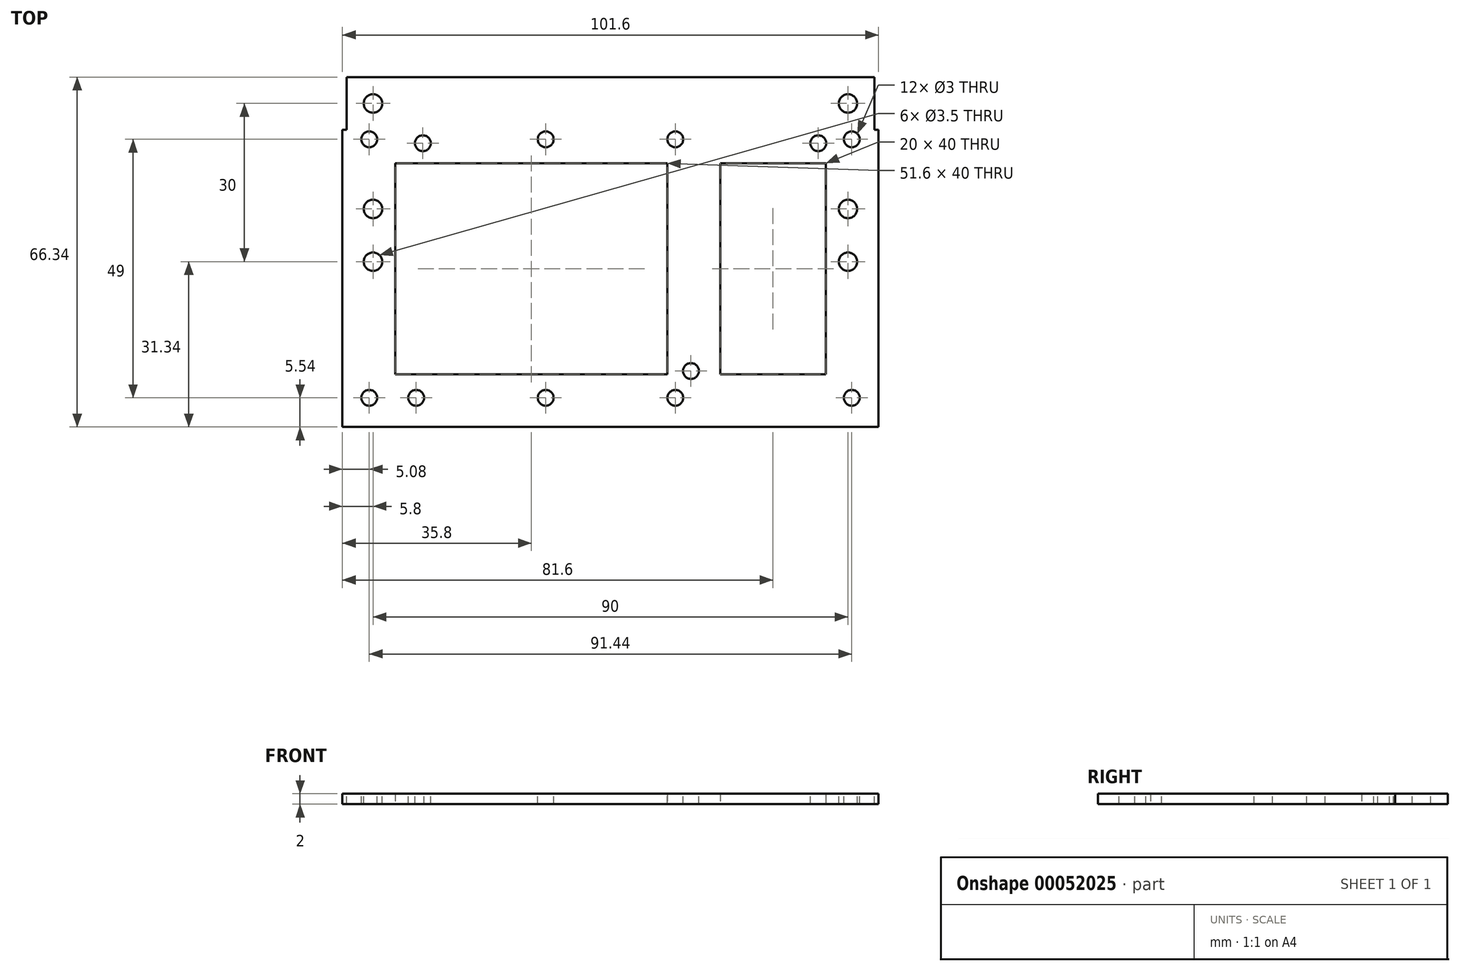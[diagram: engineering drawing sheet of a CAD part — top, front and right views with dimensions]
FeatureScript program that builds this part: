
annotation { "Feature Type Name" : "Feature", "Feature Type Description" : "" }
export const myFeature = defineFeature(function(context is Context, id is Id, definition is map)
    precondition{}
    {
        {
            var Q0;
            Q0=qCreatedBy(makeId("Top.planeOp"),FACE);
            var sketch = newSketch(context, id + "F0", { "sketchPlane" : qUnion([Q0])});
            skLineSegment(sketch, "E0.bottom", {"start": v(-50.8, 26.67) * mm, "end": v(50.8, 26.67) * mm});
            skLineSegment(sketch, "E0.top", {"start": v(-50.8, -26.67) * mm, "end": v(50.8, -26.67) * mm});
            skLineSegment(sketch, "E0.left", {"start": v(-50.8, 26.67) * mm, "end": v(-50.8, -26.67) * mm});
            skLineSegment(sketch, "E0.right", {"start": v(50.8, 26.67) * mm, "end": v(50.8, -26.67) * mm});
            skLineSegment(sketch, "E1", {"start": v(-50.8, 26.67) * mm, "end": v(50.8, -26.67) * mm, "construction": true});
            skPoint(sketch, "E2", {"position": v(0, 0) * mm});
            skSolve(sketch);
        }
        {
            var Q0;
            Q0=makeQuery(id+"F0.imprint","IMPRINT",FACE,{"disambiguationData":[TD([[makeQuery(id+"F0.imprint","IMPRINT",EDGE,{"derivedFrom":sQuery(id+"F0.wireOp",EDGE,"E0.bottom")}),-1.0]])]});
            extrude(context, id + "F1", {"entities" : qUnion([Q0]), "depth" : 2 * mm});
        }
        {
            var Q0;
            Q0=makeQuery(id+"F1.opExtrude","CAP_FACE",FACE,{"disambiguationData":[OSD([sQuery(id+"F0.wireOp",EDGE,"E0.bottom"),sQuery(id+"F0.wireOp",EDGE,"E0.top"),sQuery(id+"F0.wireOp",EDGE,"E0.left"),sQuery(id+"F0.wireOp",EDGE,"E0.right")])],"isStart":false});
            var sketch = newSketch(context, id + "F2", { "sketchPlane" : qUnion([Q0])});
            skPoint(sketch, "E3", {"position": v(-36.83, -24.13) * mm});
            skPoint(sketch, "E4", {"position": v(-35.56, 24.13) * mm});
            skPoint(sketch, "E5", {"position": v(15.24, -19.05) * mm});
            skPoint(sketch, "E6", {"position": v(45.72, -24.13) * mm});
            skPoint(sketch, "E7", {"position": v(39.37, 24.13) * mm});
            skSolve(sketch);
        }
        {
            var Q0;
            Q0=sQuery(id+"F2.wireOp",VERTEX,"E4");
            var Q1;
            Q1=sQuery(id+"F2.wireOp",VERTEX,"E7");
            var Q2;
            Q2=sQuery(id+"F2.wireOp",VERTEX,"E6");
            var Q3;
            Q3=sQuery(id+"F2.wireOp",VERTEX,"E5");
            var Q4;
            Q4=sQuery(id+"F2.wireOp",VERTEX,"E3");
            var Q5;
            Q5=makeQuery(id+"F1.opExtrude","SWEPT_BODY",BODY,{"disambiguationData":[OSD([sQuery(id+"F0.wireOp",EDGE,"E0.bottom"),sQuery(id+"F0.wireOp",EDGE,"E0.top"),sQuery(id+"F0.wireOp",EDGE,"E0.left"),sQuery(id+"F0.wireOp",EDGE,"E0.right")])]});
            hole(context, id + "F3", {"style" : HoleStyle.SIMPLE, "endStyle" : HoleEndStyle.THROUGH, "holeDiameter" : 3 * mm, "locations" : qUnion([Q0, Q1, Q2, Q3, Q4]), "scope" : qUnion([Q5]), "tappedDepth" : 12 * mm, "tapClearance" : 3});
        }
        {
            var Q0;
            Q0=makeQuery(id+"F1.opExtrude","CAP_FACE",FACE,{"disambiguationData":[OSD([sQuery(id+"F0.wireOp",EDGE,"E0.bottom"),sQuery(id+"F0.wireOp",EDGE,"E0.top"),sQuery(id+"F0.wireOp",EDGE,"E0.left"),sQuery(id+"F0.wireOp",EDGE,"E0.right")])],"isStart":false});
            var sketch = newSketch(context, id + "F4", { "sketchPlane" : qUnion([Q0])});
            skLineSegment(sketch, "E8.bottom", {"start": v(-50, 46.67) * mm, "end": v(50, 46.67) * mm});
            skLineSegment(sketch, "E8.top", {"start": v(-50, 26.67) * mm, "end": v(50, 26.67) * mm});
            skLineSegment(sketch, "E8.left", {"start": v(-50, 46.67) * mm, "end": v(-50, 26.67) * mm});
            skLineSegment(sketch, "E8.right", {"start": v(50, 46.67) * mm, "end": v(50, 26.67) * mm});
            skPoint(sketch, "E9", {"position": v(0, 26.67) * mm});
            skLineSegment(sketch, "E10.bottom", {"start": v(-50, 26.67) * mm, "end": v(-62, 26.67) * mm});
            skLineSegment(sketch, "E10.top", {"start": v(-50, 38.67) * mm, "end": v(-62, 38.67) * mm});
            skLineSegment(sketch, "E10.left", {"start": v(-50, 26.67) * mm, "end": v(-50, 38.67) * mm});
            skLineSegment(sketch, "E10.right", {"start": v(-62, 26.67) * mm, "end": v(-62, 38.67) * mm});
            skLineSegment(sketch, "E11.bottom", {"start": v(50, 26.67) * mm, "end": v(62, 26.67) * mm});
            skLineSegment(sketch, "E11.top", {"start": v(50, 38.67) * mm, "end": v(62, 38.67) * mm});
            skLineSegment(sketch, "E11.left", {"start": v(50, 26.67) * mm, "end": v(50, 38.67) * mm});
            skLineSegment(sketch, "E11.right", {"start": v(62, 26.67) * mm, "end": v(62, 38.67) * mm});
            skLineSegment(sketch, "E12.bottom", {"start": v(-50.8, -26.67) * mm, "end": v(50.8, -26.67) * mm});
            skLineSegment(sketch, "E12.top", {"start": v(-50.8, -29.67) * mm, "end": v(50.8, -29.67) * mm});
            skLineSegment(sketch, "E12.left", {"start": v(-50.8, -26.67) * mm, "end": v(-50.8, -29.67) * mm});
            skLineSegment(sketch, "E12.right", {"start": v(50.8, -26.67) * mm, "end": v(50.8, -29.67) * mm});
            skLineSegment(sketch, "E13.top", {"start": v(-50, 36.67) * mm, "end": v(50, 36.67) * mm});
            skLineSegment(sketch, "E13.left", {"start": v(-50, 26.67) * mm, "end": v(-50, 36.67) * mm});
            skLineSegment(sketch, "E13.right", {"start": v(50, 26.67) * mm, "end": v(50, 36.67) * mm});
            skSolve(sketch);
        }
        {
            var Q0;
            Q0=makeQuery(id+"F4.imprint","IMPRINT",FACE,{"disambiguationData":[TD([[makeQuery(id+"F4.imprint","IMPRINT",EDGE,{"derivedFrom":sQuery(id+"F4.wireOp",EDGE,"E12.bottom")}),-1.0]])]});
            var Q1;
            Q1=makeQuery(id+"F4.imprint","IMPRINT",FACE,{"disambiguationData":[TD([[makeQuery(id+"F4.imprint","IMPRINT",EDGE,{"derivedFrom":sQuery(id+"F4.wireOp",EDGE,"E8.top")}),1.0]])]});
            var Q2;
            Q2=makeQuery(id+"F1.opExtrude","CAP_FACE",FACE,{"disambiguationData":[OSD([sQuery(id+"F0.wireOp",EDGE,"E0.bottom"),sQuery(id+"F0.wireOp",EDGE,"E0.top"),sQuery(id+"F0.wireOp",EDGE,"E0.left"),sQuery(id+"F0.wireOp",EDGE,"E0.right")])],"isStart":true});
            extrude(context, id + "F5", {"entities" : qUnion([Q0, Q1]), "operationType" : NewBodyOperationType.ADD, "endBound" : BoundingType.UP_TO_SURFACE, "oppositeDirection" : true, "endBoundEntityFace" : qUnion([Q2]), "depth" : 25 * mm});
        }
        {
            var Q0;
            Q0=makeQuery(id+"F5.boolean.opBoolean","MERGE",FACE,{"derivedFrom":[makeQuery(id+"F1.opExtrude","CAP_FACE",FACE,{"disambiguationData":[OSD([sQuery(id+"F0.wireOp",EDGE,"E0.bottom"),sQuery(id+"F0.wireOp",EDGE,"E0.top"),sQuery(id+"F0.wireOp",EDGE,"E0.left"),sQuery(id+"F0.wireOp",EDGE,"E0.right")])],"isStart":false}),makeQuery(id+"F5.opExtrude","CAP_FACE",FACE,{"disambiguationData":[OSD([sQuery(id+"F4.wireOp",EDGE,"E8.bottom"),sQuery(id+"F4.wireOp",EDGE,"E8.top"),sQuery(id+"F4.wireOp",EDGE,"E8.left"),sQuery(id+"F4.wireOp",EDGE,"E8.right"),sQuery(id+"F4.wireOp",EDGE,"E10.bottom"),sQuery(id+"F4.wireOp",EDGE,"E10.top"),sQuery(id+"F4.wireOp",EDGE,"E10.right"),sQuery(id+"F4.wireOp",EDGE,"E11.bottom"),sQuery(id+"F4.wireOp",EDGE,"E11.top"),sQuery(id+"F4.wireOp",EDGE,"E11.right")])],"isStart":true})]});
            var sketch = newSketch(context, id + "F6", { "sketchPlane" : qUnion([Q0])});
            skLineSegment(sketch, "E14.bottom", {"start": v(-50, 26.67) * mm, "end": v(50, 26.67) * mm});
            skLineSegment(sketch, "E14.top", {"start": v(-50, 36.67) * mm, "end": v(50, 36.67) * mm});
            skLineSegment(sketch, "E14.left", {"start": v(-50, 26.67) * mm, "end": v(-50, 36.67) * mm});
            skLineSegment(sketch, "E14.right", {"start": v(50, 26.67) * mm, "end": v(50, 36.67) * mm});
            skLineSegment(sketch, "E15.bottom", {"start": v(-50, 26.67) * mm, "end": v(-40, 26.67) * mm});
            skLineSegment(sketch, "E15.top", {"start": v(-50, 36.67) * mm, "end": v(-40, 36.67) * mm});
            skLineSegment(sketch, "E15.right", {"start": v(-40, 26.67) * mm, "end": v(-40, 36.67) * mm});
            skLineSegment(sketch, "E16.bottom", {"start": v(50, 26.67) * mm, "end": v(40, 26.67) * mm});
            skLineSegment(sketch, "E16.top", {"start": v(50, 36.67) * mm, "end": v(40, 36.67) * mm});
            skLineSegment(sketch, "E16.right", {"start": v(40, 26.67) * mm, "end": v(40, 36.67) * mm});
            skLineSegment(sketch, "E17", {"start": v(-50, 36.67) * mm, "end": v(-40, 26.67) * mm});
            skLineSegment(sketch, "E18", {"start": v(40, 26.67) * mm, "end": v(50, 36.67) * mm});
            skPoint(sketch, "E19", {"position": v(-45, 31.67) * mm});
            skPoint(sketch, "E20", {"position": v(45, 31.67) * mm});
            skPoint(sketch, "E21.0.1.0", {"position": v(-45, 21.67) * mm});
            skPoint(sketch, "E21.0.1.1", {"position": v(45, 21.67) * mm});
            skPoint(sketch, "E21.0.2.0", {"position": v(-45, 11.67) * mm});
            skPoint(sketch, "E21.0.2.1", {"position": v(45, 11.67) * mm});
            skPoint(sketch, "E21.0.3.0", {"position": v(-45, 1.67) * mm});
            skPoint(sketch, "E21.0.3.1", {"position": v(45, 1.67) * mm});
            skLineSegment(sketch, "E21.direction1", {"start": v(-45, 31.67) * mm, "end": v(-20, 31.67) * mm, "construction": true});
            skLineSegment(sketch, "E21.direction2", {"start": v(-45, 31.67) * mm, "end": v(-45, 21.67) * mm, "construction": true});
            skSolve(sketch);
        }
        {
            var Q0;
            Q0=sQuery(id+"F6.wireOp",VERTEX,"E19");
            var Q1;
            Q1=sQuery(id+"F6.wireOp",VERTEX,"E20");
            var Q2;
            Q2=sQuery(id+"F6.wireOp",VERTEX,"E21.0.2.0");
            var Q3;
            Q3=sQuery(id+"F6.wireOp",VERTEX,"E21.0.3.0");
            var Q4;
            Q4=sQuery(id+"F6.wireOp",VERTEX,"E21.0.2.1");
            var Q5;
            Q5=sQuery(id+"F6.wireOp",VERTEX,"E21.0.3.1");
            var Q6;
            Q6=makeQuery(id+"F1.opExtrude","SWEPT_BODY",BODY,{"disambiguationData":[OSD([sQuery(id+"F0.wireOp",EDGE,"E0.bottom"),sQuery(id+"F0.wireOp",EDGE,"E0.top"),sQuery(id+"F0.wireOp",EDGE,"E0.left"),sQuery(id+"F0.wireOp",EDGE,"E0.right")])]});
            hole(context, id + "F7", {"style" : HoleStyle.SIMPLE, "endStyle" : HoleEndStyle.THROUGH, "holeDiameter" : 3.5 * mm, "locations" : qUnion([Q0, Q1, Q2, Q3, Q4, Q5]), "scope" : qUnion([Q6]), "tappedDepth" : 12 * mm, "tapClearance" : 3});
        }
        {
            var Q0;
            {var subQ0=sQuery(id+"F0.wireOp",EDGE,"E0.right");var subQ1=sQuery(id+"F0.wireOp",EDGE,"E0.left");var subQ2=sQuery(id+"F0.wireOp",EDGE,"E0.top");var subQ3=sQuery(id+"F0.wireOp",EDGE,"E0.bottom");var subQ4=sQuery(id+"F4.wireOp",EDGE,"E12.left");var subQ5=sQuery(id+"F4.wireOp",EDGE,"E13.top");var subQ6=sQuery(id+"F4.wireOp",EDGE,"E12.top");var subQ7=sQuery(id+"F4.wireOp",EDGE,"E12.right");var subQ8=sQuery(id+"F4.wireOp",EDGE,"E10.left");var subQ9=sQuery(id+"F4.wireOp",EDGE,"E11.top");var subQ10=sQuery(id+"F4.wireOp",EDGE,"E8.top");var subQ11=sQuery(id+"F4.wireOp",EDGE,"E11.left");var subQ12=sQuery(id+"F4.wireOp",EDGE,"E11.bottom");var subQ13=sQuery(id+"F4.wireOp",EDGE,"E10.top");var subQ14=sQuery(id+"F4.wireOp",EDGE,"E10.bottom");var subQ15=makeQuery(id+"F5.opExtrude","CAP_FACE",FACE,{"disambiguationData":[OSD([subQ14,subQ13,subQ8,sQuery(id+"F4.wireOp",EDGE,"E10.right"),subQ12,subQ9,subQ11,sQuery(id+"F4.wireOp",EDGE,"E11.right"),subQ10,subQ5])],"isStart":true});var subQ16=makeQuery(id+"F5.opExtrude","CAP_FACE",FACE,{"disambiguationData":[OSD([sQuery(id+"F4.wireOp",EDGE,"E12.bottom"),subQ6,subQ4,subQ7])],"isStart":true});var subQ17=makeQuery(id+"F1.opExtrude","CAP_FACE",FACE,{"disambiguationData":[OSD([subQ3,subQ2,subQ1,subQ0])],"isStart":false});Q0=makeQuery(id+"FY9umivuI4225pz_1.boolean.opBoolean","SPLIT",FACE,{"disambiguationData":[TD([subQ17,makeQuery(id+"F1.opExtrude","SWEPT_FACE",FACE,{"disambiguationData":[OSD([subQ1])]}),makeQuery(id+"F1.opExtrude","SWEPT_FACE",FACE,{"disambiguationData":[OSD([subQ0])]}),subQ15,makeQuery(id+"F5.opExtrude","SWEPT_FACE",FACE,{"disambiguationData":[OSD([subQ14,subQ12,subQ10])]}),makeQuery(id+"F5.opExtrude","SWEPT_FACE",FACE,{"disambiguationData":[OSD([subQ13])]}),makeQuery(id+"F5.opExtrude","SWEPT_FACE",FACE,{"disambiguationData":[OSD([subQ8])]}),makeQuery(id+"F5.opExtrude","SWEPT_FACE",FACE,{"disambiguationData":[OSD([subQ9])]}),makeQuery(id+"F5.opExtrude","SWEPT_FACE",FACE,{"disambiguationData":[OSD([subQ11])]}),subQ16,makeQuery(id+"F5.opExtrude","SWEPT_FACE",FACE,{"disambiguationData":[OSD([subQ6])]}),makeQuery(id+"F5.opExtrude","SWEPT_FACE",FACE,{"disambiguationData":[OSD([subQ4])]}),makeQuery(id+"F5.opExtrude","SWEPT_FACE",FACE,{"disambiguationData":[OSD([subQ7])]}),makeQuery(id+"F5.opExtrude","SWEPT_FACE",FACE,{"disambiguationData":[OSD([subQ5])]}),makeQuery(id+"FAB3qb6dTxeGC13_1.opChamfer","BLEND_FACE",FACE,{"disambiguationData":[OSD([subQ3,subQ2,subQ1,subQ0,sQuery(id+"F3.hole-0.sketch.wireOp",EDGE,"core_line_2")])]}),makeQuery(id+"FAB3qb6dTxeGC13_1.opChamfer","BLEND_FACE",FACE,{"disambiguationData":[OSD([subQ3,subQ2,subQ1,subQ0,sQuery(id+"F3.hole-1.sketch.wireOp",EDGE,"core_line_2")])]}),makeQuery(id+"FAB3qb6dTxeGC13_1.opChamfer","BLEND_FACE",FACE,{"disambiguationData":[OSD([subQ3,subQ2,subQ1,subQ0,sQuery(id+"F3.hole-2.sketch.wireOp",EDGE,"core_line_2")])]}),makeQuery(id+"FAB3qb6dTxeGC13_1.opChamfer","BLEND_FACE",FACE,{"disambiguationData":[OSD([subQ3,subQ2,subQ1,subQ0,sQuery(id+"F3.hole-3.sketch.wireOp",EDGE,"core_line_2")])]}),makeQuery(id+"FAB3qb6dTxeGC13_1.opChamfer","BLEND_FACE",FACE,{"disambiguationData":[OSD([subQ3,subQ2,subQ1,subQ0,sQuery(id+"F3.hole-4.sketch.wireOp",EDGE,"core_line_2")])]}),makeQuery(id+"F7.hole-0.boolean.opBoolean","COPY",FACE,{"derivedFrom":makeQuery(id+"F7.hole-0.opRevolve","SWEPT_FACE",FACE,{"disambiguationData":[OSD([sQuery(id+"F7.hole-0.sketch.wireOp",EDGE,"core_line_2")])]})}),makeQuery(id+"F7.hole-1.boolean.opBoolean","COPY",FACE,{"derivedFrom":makeQuery(id+"F7.hole-1.opRevolve","SWEPT_FACE",FACE,{"disambiguationData":[OSD([sQuery(id+"F7.hole-1.sketch.wireOp",EDGE,"core_line_2")])]})}),makeQuery(id+"FY9umivuI4225pz_1.opExtrude","SWEPT_FACE",FACE,{"disambiguationData":[OSD([sQuery(id+"FG0PhvfrKBBsj4x_1.wireOp",EDGE,"L8qLSeHA-hHTf-AzzE-YKTA-MX94CUHkupDC")])]}),makeQuery(id+"FY9umivuI4225pz_1.opExtrude","SWEPT_FACE",FACE,{"disambiguationData":[OSD([sQuery(id+"FG0PhvfrKBBsj4x_1.wireOp",EDGE,"lvMhVdlb-QRLn-6RCz-rsW7-6NAXlfRSvE0M")])]})])],"derivedFrom":makeQuery(id+"F5.boolean.opBoolean","MERGE",FACE,{"derivedFrom":[subQ17,subQ15,subQ16]})});}
            var sketch = newSketch(context, id + "F8", { "sketchPlane" : qUnion([Q0])});
            skLineSegment(sketch, "E22.bottom", {"start": v(-12.28, 24.87) * mm, "end": v(45.72, 24.87) * mm});
            skLineSegment(sketch, "E22.top", {"start": v(-12.28, -24.13) * mm, "end": v(45.72, -24.13) * mm});
            skLineSegment(sketch, "E22.left", {"start": v(-12.28, 24.87) * mm, "end": v(-12.28, -24.13) * mm});
            skLineSegment(sketch, "E22.right", {"start": v(45.72, 24.87) * mm, "end": v(45.72, -24.13) * mm});
            skLineSegment(sketch, "E23.MirrorCS", {"start": v(12.28, 24.87) * mm, "end": v(12.28, -24.13) * mm});
            skLineSegment(sketch, "E24.MirrorCS", {"start": v(-45.72, 24.87) * mm, "end": v(-45.72, -24.13) * mm});
            skSolve(sketch);
        }
        {
            var Q0;
            Q0=sQuery(id+"F8.wireOp",VERTEX,"E24.MirrorCS.end");
            var Q1;
            Q1=sQuery(id+"F8.wireOp",VERTEX,"E24.MirrorCS.start");
            var Q2;
            Q2=sQuery(id+"F8.wireOp",VERTEX,"E22.bottom.start");
            var Q3;
            Q3=sQuery(id+"F8.wireOp",VERTEX,"E23.MirrorCS.start");
            var Q4;
            Q4=sQuery(id+"F8.wireOp",VERTEX,"E23.MirrorCS.end");
            var Q5;
            Q5=sQuery(id+"F8.wireOp",VERTEX,"E22.top.start");
            var Q6;
            Q6=sQuery(id+"F8.wireOp",VERTEX,"E22.bottom.end");
            var Q7;
            Q7=makeQuery(id+"F1.opExtrude","SWEPT_BODY",BODY,{"disambiguationData":[OSD([sQuery(id+"F0.wireOp",EDGE,"E0.bottom"),sQuery(id+"F0.wireOp",EDGE,"E0.top"),sQuery(id+"F0.wireOp",EDGE,"E0.left"),sQuery(id+"F0.wireOp",EDGE,"E0.right")])]});
            hole(context, id + "F9", {"style" : HoleStyle.SIMPLE, "endStyle" : HoleEndStyle.THROUGH, "holeDiameter" : 3 * mm, "locations" : qUnion([Q0, Q1, Q2, Q3, Q4, Q5, Q6]), "scope" : qUnion([Q7]), "tappedDepth" : 12 * mm, "tapClearance" : 3});
        }
        {
            var Q0;
            {var subQ0=sQuery(id+"F0.wireOp",EDGE,"E0.right");var subQ1=sQuery(id+"F0.wireOp",EDGE,"E0.left");var subQ2=sQuery(id+"F0.wireOp",EDGE,"E0.top");var subQ3=sQuery(id+"F0.wireOp",EDGE,"E0.bottom");Q0=makeQuery(id+"F5.boolean.opBoolean","MERGE",FACE,{"derivedFrom":[makeQuery(id+"F1.opExtrude","CAP_FACE",FACE,{"disambiguationData":[OSD([subQ3,subQ2,subQ1,subQ0])],"isStart":true}),makeQuery(id+"F5.opExtrude","CAP_FACE",FACE,{"disambiguationData":[OSD([subQ3,subQ2,subQ1,subQ0]),ownerDisambiguation([makeQuery(id+"F5.opExtrude","SWEPT_BODY",BODY,{"disambiguationData":[OSD([sQuery(id+"F4.wireOp",EDGE,"E10.bottom"),sQuery(id+"F4.wireOp",EDGE,"E10.top"),sQuery(id+"F4.wireOp",EDGE,"E10.left"),sQuery(id+"F4.wireOp",EDGE,"E10.right"),sQuery(id+"F4.wireOp",EDGE,"E11.bottom"),sQuery(id+"F4.wireOp",EDGE,"E11.top"),sQuery(id+"F4.wireOp",EDGE,"E11.left"),sQuery(id+"F4.wireOp",EDGE,"E11.right"),sQuery(id+"F4.wireOp",EDGE,"E8.top"),sQuery(id+"F4.wireOp",EDGE,"E13.top")])]})])],"isStart":false}),makeQuery(id+"F5.opExtrude","CAP_FACE",FACE,{"disambiguationData":[OSD([subQ3,subQ2,subQ1,subQ0]),ownerDisambiguation([makeQuery(id+"F5.opExtrude","SWEPT_BODY",BODY,{"disambiguationData":[OSD([sQuery(id+"F4.wireOp",EDGE,"E12.bottom"),sQuery(id+"F4.wireOp",EDGE,"E12.top"),sQuery(id+"F4.wireOp",EDGE,"E12.left"),sQuery(id+"F4.wireOp",EDGE,"E12.right")])]})])],"isStart":false})]});}
            var sketch = newSketch(context, id + "F10", { "sketchPlane" : qUnion([Q0])});
            skLineSegment(sketch, "E25.bottom", {"start": v(-40.8, 19.67) * mm, "end": v(10.8, 19.67) * mm});
            skLineSegment(sketch, "E25.top", {"start": v(-40.8, -20.33) * mm, "end": v(10.8, -20.33) * mm});
            skLineSegment(sketch, "E25.left", {"start": v(-40.8, 19.67) * mm, "end": v(-40.8, -20.33) * mm});
            skLineSegment(sketch, "E25.right", {"start": v(10.8, 19.67) * mm, "end": v(10.8, -20.33) * mm});
            skLineSegment(sketch, "E26.bottom", {"start": v(20.8, 19.67) * mm, "end": v(40.8, 19.67) * mm});
            skLineSegment(sketch, "E26.top", {"start": v(20.8, -20.33) * mm, "end": v(40.8, -20.33) * mm});
            skLineSegment(sketch, "E26.left", {"start": v(20.8, 19.67) * mm, "end": v(20.8, -20.33) * mm});
            skLineSegment(sketch, "E26.right", {"start": v(40.8, 19.67) * mm, "end": v(40.8, -20.33) * mm});
            skSolve(sketch);
        }
        {
            var Q0;
            Q0=makeQuery(id+"F10.imprint","IMPRINT",FACE,{"disambiguationData":[TD([[makeQuery(id+"F10.imprint","IMPRINT",EDGE,{"derivedFrom":sQuery(id+"F10.wireOp",EDGE,"E25.bottom")}),-1.0]])]});
            var Q1;
            Q1=makeQuery(id+"F10.imprint","IMPRINT",FACE,{"disambiguationData":[TD([[makeQuery(id+"F10.imprint","IMPRINT",EDGE,{"derivedFrom":sQuery(id+"F10.wireOp",EDGE,"E26.bottom")}),-1.0]])]});
            extrude(context, id + "F11", {"entities" : qUnion([Q0, Q1]), "operationType" : NewBodyOperationType.REMOVE, "endBound" : BoundingType.THROUGH_ALL, "oppositeDirection" : true, "depth" : 25 * mm});
        }
    });
